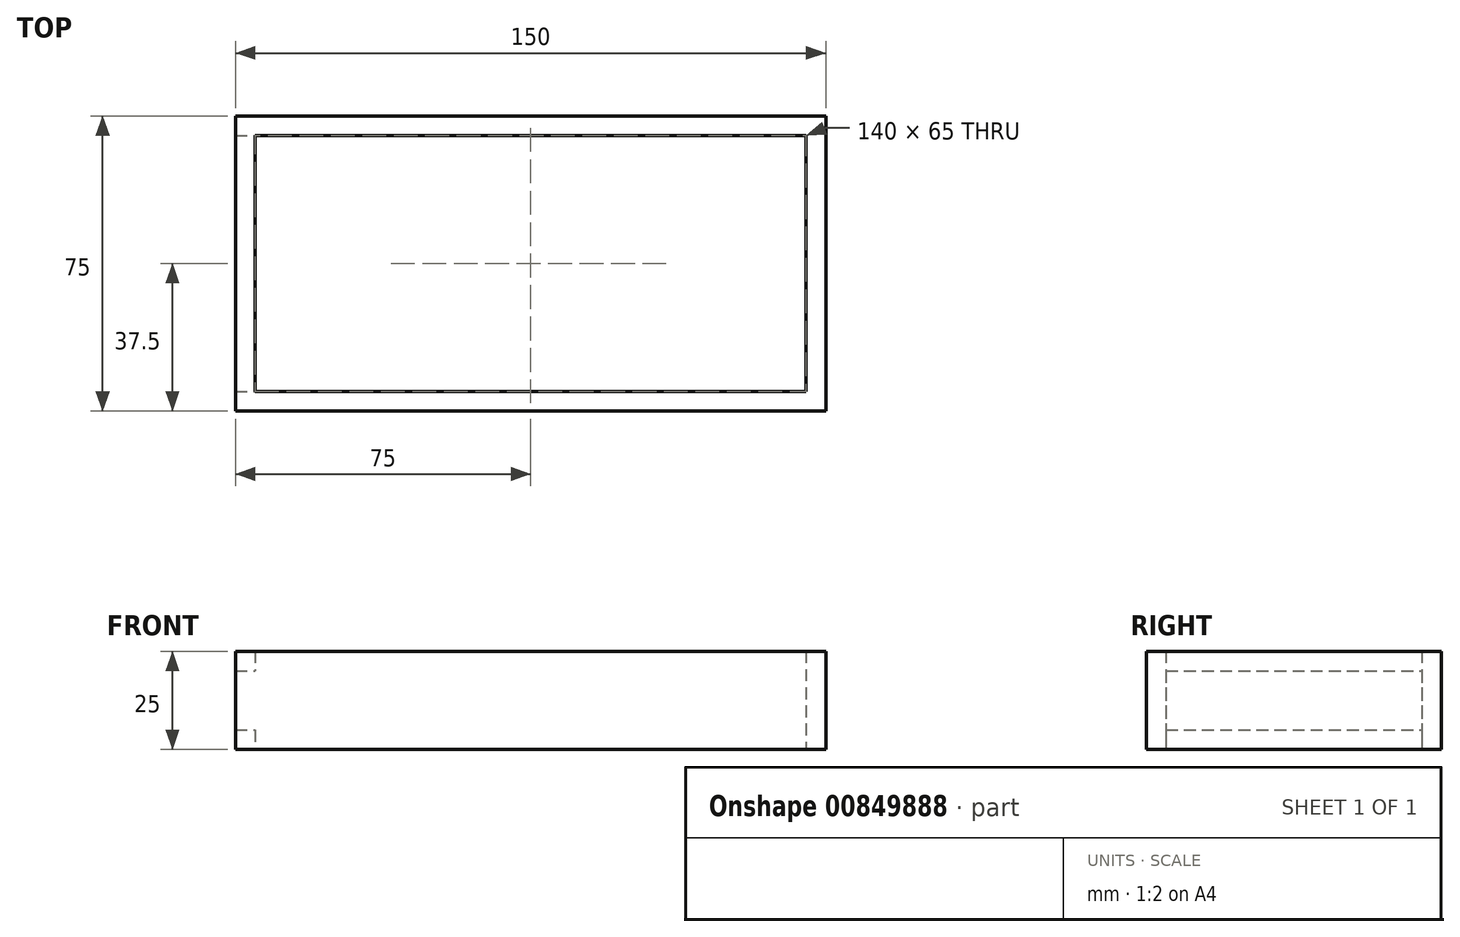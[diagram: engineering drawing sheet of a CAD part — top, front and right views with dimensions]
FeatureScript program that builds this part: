
annotation { "Feature Type Name" : "Feature", "Feature Type Description" : "" }
export const myFeature = defineFeature(function(context is Context, id is Id, definition is map)
    precondition{}
    {
        {
            var Q0;
            Q0=qCreatedBy(makeId("Top.planeOp"),FACE);
            var sketch = newSketch(context, id + "F0", { "sketchPlane" : qUnion([Q0])});
            skLineSegment(sketch, "E0.bottom", {"start": v(-75, -37.5) * mm, "end": v(75, -37.5) * mm});
            skLineSegment(sketch, "E0.top", {"start": v(-75, 37.5) * mm, "end": v(75, 37.5) * mm});
            skLineSegment(sketch, "E0.left", {"start": v(-75, -37.5) * mm, "end": v(-75, 37.5) * mm});
            skLineSegment(sketch, "E0.right", {"start": v(75, -37.5) * mm, "end": v(75, 37.5) * mm});
            skPoint(sketch, "E0.middle", {"position": v(0, 0) * mm});
            skSolve(sketch);
        }
        {
            var Q0;
            Q0 = qSketchRegion(id + "F0", true);
            extrude(context, id + "F1", {"entities" : qUnion([Q0]), "depth" : 25 * mm, "offsetDistance" : 25 * mm});
        }
        {
            var Q0;
            Q0=makeQuery(id+"F1.opExtrude","SWEPT_FACE",FACE,{"disambiguationData":[OSD([sQuery(id+"F0.wireOp",EDGE,"E0.left")])]});
            shell(context, id + "F2", {"entities" : qUnion([Q0]), "thickness" : 5 * mm});
        }
        {
            var Q0;
            Q0=qCreatedBy(makeId("Top.planeOp"),FACE);
            var sketch = newSketch(context, id + "F3", { "sketchPlane" : qUnion([Q0])});
            skLineSegment(sketch, "E1.0", {"start": v(70, 32.5) * mm, "end": v(-70, 32.5) * mm});
            skLineSegment(sketch, "E1.1", {"start": v(70, -32.5) * mm, "end": v(70, 32.5) * mm});
            skLineSegment(sketch, "E1.2", {"start": v(-70, -32.5) * mm, "end": v(70, -32.5) * mm});
            skLineSegment(sketch, "E1.3", {"start": v(-70, 32.5) * mm, "end": v(-70, -32.5) * mm});
            skSolve(sketch);
        }
        {
            var Q0;
            Q0 = qSketchRegion(id + "F3", true);
            extrude(context, id + "F4", {"entities" : qUnion([Q0]), "operationType" : NewBodyOperationType.REMOVE, "endBound" : BoundingType.THROUGH_ALL, "depth" : 25 * mm, "offsetDistance" : 25 * mm});
        }
    });
